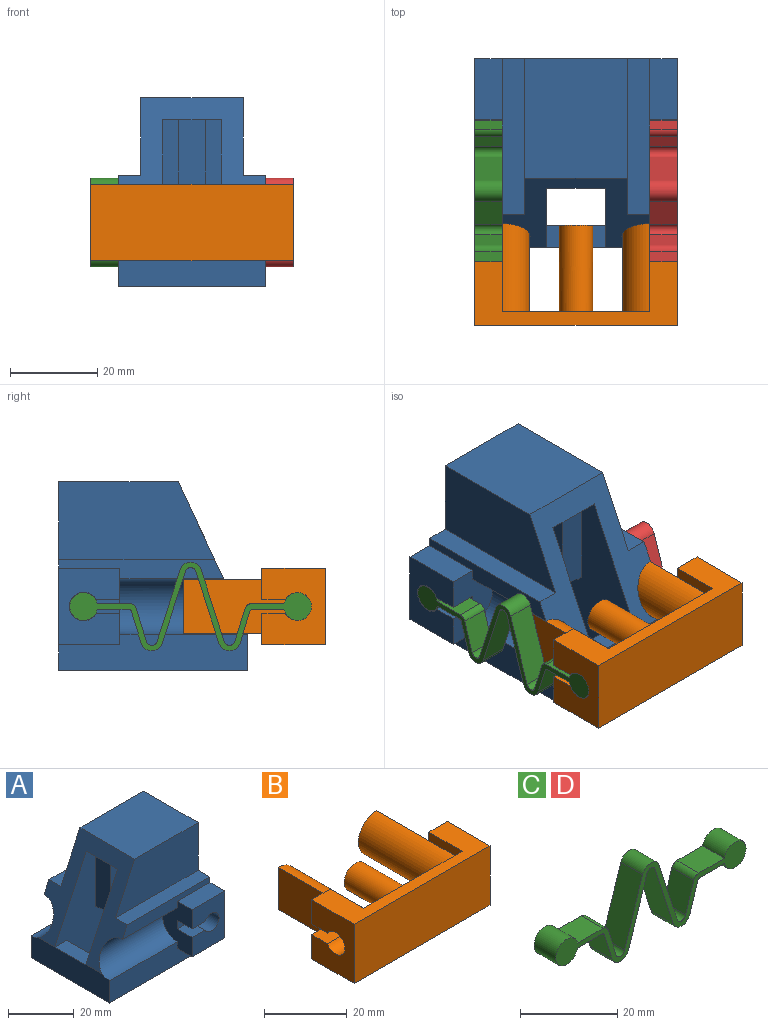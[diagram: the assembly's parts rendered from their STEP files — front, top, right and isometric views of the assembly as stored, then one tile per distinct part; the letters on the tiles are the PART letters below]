
ASSEMBLY  parts=4 mates=6
PART A: 44 faces, bbox 43.2x46.4x43.2 mm
  f0: plane 17.53x12.7mm, normal (-1,0,0), area 154.5mm2, adj f1,f4,f29,f37,f38,f39,f40,f42
  f1: plane 43.23x8.26mm, normal (0,-1,0), area 323mm2, adj f0,f14,f16,f17,f29,f38
  f2: plane 37.72x4.45mm, normal (0,1,0), area 129.2mm2, adj f3,f14,f24,f26,f27,f30
  f3: plane 34.04x33.71mm, normal (-0.91,0,0.42), area 503.5mm2, adj f2,f4,f7,f8,f9,f10,f12,f13
  f4: plane 37.72x4.45mm, normal (0,-1,0), area 129.2mm2, adj f0,f3,f14,f28,f29,f37
  f5: plane 19.05x6.35mm, normal (-1,0,0), area 119.5mm2, adj f6,f13,f18,f19,f21,f23
  f6: plane 8.26x0.99mm, normal (0,0,-1), area 8.2mm2, adj f5,f18,f20,f23
  f7: plane 35.65x17.78mm, normal (0,-1,0), area 560.1mm2, adj f3,f8,f14,f28
  f8: plane 27.36x23.55mm, normal (0,0,1), area 644.1mm2, adj f3,f7,f9,f14
  f9: plane 35.65x17.78mm, normal (0,1,0), area 560.1mm2, adj f3,f8,f14,f24
  f10: plane 38.15x38.1mm, normal (0,1,0), area 1211.5mm2, adj f3,f11,f13,f15,f17,f22
  f11: plane 13.39x9.14mm, normal (1,0,0), area 122.3mm2, adj f10,f12,f17,f22
  f12: plane 38.15x38.1mm, normal (0,-1,0), area 1211.5mm2, adj f3,f11,f13,f15,f17,f22
  f13: plane 24.64x13.39mm, normal (0,0,-1), area 277.5mm2, adj f3,f5,f10,f12,f15,f18,f19,f20
  f14: plane 46.41x43.18mm, normal (1,0,0), area 1497.4mm2, adj f1,f2,f4,f7,f8,f9,f17,f24
  f15: plane 38.1x13.39mm, normal (-1,0,0), area 510mm2, adj f10,f12,f13,f17
  f16: plane 33.71x9.14mm, normal (-1,0,0), area 304.1mm2, adj f1,f3,f17,f22,f25,f26,f29
  f17: plane 43.23x33.71mm, normal (0,0,-1), area 1014.4mm2, adj f1,f10,f11,f12,f14,f15,f16,f25
  f18: plane 19.05x8.26mm, normal (0,-1,0), area 157.3mm2, adj f5,f6,f13,f20
  f19: plane 19.05x8.26mm, normal (0,1,0), area 157.3mm2, adj f5,f13,f20,f21
  f20: plane 19.05x6.35mm, normal (1,0,0), area 119.5mm2, adj f6,f13,f18,f19,f21,f23
  f21: plane 8.26x0.99mm, normal (0,0,-1), area 8.2mm2, adj f5,f19,f20,f23
  f22: plane 13.39x5.08mm, normal (0,0,1), area 68mm2, adj f10,f11,f12,f16
  f23: cylinder r=4.95mm len=8.26mm, axis (-1,0,0), area 37.4mm2, adj f5,f6,f20,f21
  f24: plane 35.65x5.08mm, normal (0,0,1), area 181.1mm2, adj f2,f3,f9,f14
  f25: plane 43.23x8.26mm, normal (0,1,0), area 323mm2, adj f14,f16,f17,f26,f27,f31
  f26: cylinder r=6.35mm len=29.21mm, axis (-1,0,0), area 530.9mm2, adj f2,f3,f16,f25,f27
  f27: plane 17.53x12.7mm, normal (-1,0,0), area 154.5mm2, adj f2,f25,f26,f30,f31,f32,f33,f34
  f28: plane 35.65x5.08mm, normal (0,0,1), area 181.1mm2, adj f3,f4,f7,f14
  f29: cylinder r=6.35mm len=29.21mm, axis (-1,0,0), area 530.9mm2, adj f0,f1,f3,f4,f16
  f30: plane 14.02x6.35mm, normal (0,0,1), area 89mm2, adj f2,f14,f27,f32
  f31: plane 14.02x6.35mm, normal (0,0,-1), area 89mm2, adj f14,f25,f27,f32
  f32: plane 17.53x14.02mm, normal (0,1,0), area 195.4mm2, adj f14,f27,f30,f31,f34,f35,f36
  f33: plane 11.6x6.58mm, normal (0,1,0), area 50.3mm2, adj f27,f34,f35,f36
  f34: plane 6.35x5.43mm, normal (0,0,1), area 34.4mm2, adj f27,f32,f33,f35
  f35: cylinder r=3.29mm len=6.58mm, axis (0,1,0), area 110.2mm2, adj f32,f33,f34,f36
  f36: plane 6.35x5.43mm, normal (0,0,-1), area 34.4mm2, adj f27,f32,f33,f35
  f37: plane 14.02x6.35mm, normal (0,0,1), area 89mm2, adj f0,f4,f14,f39
  f38: plane 14.02x6.35mm, normal (0,0,-1), area 89mm2, adj f0,f1,f14,f39
  f39: plane 17.53x14.02mm, normal (0,-1,0), area 195.4mm2, adj f0,f14,f37,f38,f40,f41,f42
  f40: plane 6.35x5.43mm, normal (0,0,1), area 34.4mm2, adj f0,f39,f41,f43
  f41: cylinder r=3.29mm len=6.58mm, axis (0,-1,0), area 110.2mm2, adj f39,f40,f42,f43
  f42: plane 6.35x5.43mm, normal (0,0,-1), area 34.4mm2, adj f0,f39,f41,f43
  f43: plane 11.6x6.58mm, normal (0,-1,0), area 50.3mm2, adj f0,f40,f41,f42
PART B: 28 faces, bbox 46.4x32.4x17.5 mm
  f0: plane 46.41x14.54mm, normal (0,0,1), area 291.6mm2, adj f2,f3,f4,f11,f14,f15,f18,f24
  f1: plane 11.36x2.54mm, normal (-1,0,0), area 28.9mm2, adj f5,f12,f15,f25
  f2: plane 11.36x2.54mm, normal (-1,0,0), area 28.9mm2, adj f0,f12,f15,f24
  f3: plane 17.53x14.54mm, normal (1,0,0), area 206.7mm2, adj f0,f5,f14,f20,f21,f22,f24,f25
  f4: plane 11.36x2.54mm, normal (1,0,0), area 28.9mm2, adj f0,f10,f15,f18
  f5: plane 46.41x14.54mm, normal (0,0,-1), area 291.6mm2, adj f1,f3,f6,f11,f14,f15,f19,f25
  f6: plane 11.36x2.54mm, normal (1,0,0), area 28.9mm2, adj f5,f10,f15,f19
  f7: plane 12.45x6.22mm, normal (0,1,0), area 60.8mm2, adj f10,f17
  f8: plane 6.35x5.44mm, normal (0,0,1), area 34.5mm2, adj f11,f16,f17,f19
  f9: plane 6.35x5.44mm, normal (0,0,-1), area 34.5mm2, adj f11,f16,f17,f18
  f10: cylinder r=6.22mm len=29.21mm, axis (0,1,0), area 571.1mm2, adj f4,f6,f7,f15,f17
  f11: plane 17.53x14.54mm, normal (-1,0,0), area 206.7mm2, adj f0,f5,f8,f9,f14,f16,f18,f19
  f12: cylinder r=6.22mm len=29.21mm, axis (0,1,0), area 571.1mm2, adj f1,f2,f13,f15,f23
  f13: plane 12.45x6.22mm, normal (0,1,0), area 60.8mm2, adj f12,f23
  f14: plane 46.41x17.53mm, normal (0,-1,0), area 813.3mm2, adj f0,f3,f5,f11
  f15: plane 33.71x17.53mm, normal (0,1,0), area 423.5mm2, adj f0,f1,f2,f4,f5,f6,f10,f12
  f16: cylinder r=3.17mm len=6.35mm, axis (-1,0,0), area 105.6mm2, adj f8,f9,f11,f17
  f17: plane 29.21x12.45mm, normal (-1,0,0), area 270.2mm2, adj f7,f8,f9,f10,f16,f18,f19
  f18: plane 7.18x6.35mm, normal (0,1,0), area 45.6mm2, adj f0,f4,f9,f11,f17
  f19: plane 7.18x6.35mm, normal (0,1,0), area 45.6mm2, adj f5,f6,f8,f11,f17
  f20: plane 6.35x5.44mm, normal (0,0,1), area 34.5mm2, adj f3,f22,f23,f25
  f21: plane 6.35x5.44mm, normal (0,0,-1), area 34.5mm2, adj f3,f22,f23,f24
  f22: cylinder r=3.17mm len=6.35mm, axis (1,0,0), area 105.6mm2, adj f3,f20,f21,f23
  f23: plane 29.21x12.45mm, normal (1,0,0), area 270.2mm2, adj f12,f13,f20,f21,f22,f24,f25
  f24: plane 7.18x6.35mm, normal (0,1,0), area 45.6mm2, adj f0,f2,f3,f21,f23
  f25: plane 7.18x6.35mm, normal (0,1,0), area 45.6mm2, adj f1,f3,f5,f20,f23
  f26: cylinder r=3.81mm len=19.69mm, axis (0,-1,0), area 471.2mm2, adj f15,f27
  f27: plane 7.62x7.62mm, normal (0,1,0), area 45.6mm2, adj f26
PART C: 26 faces, bbox 55.3x6.4x20.3 mm
  f0: cylinder r=3.17mm len=6.35mm, axis (0,1,0), area 118.6mm2, adj f1,f23,f24,f25
  f1: plane 7.09x6.35mm, normal (0,0,-1), area 45mm2, adj f0,f2,f24,f25
  f2: cylinder r=0.76mm len=6.35mm, axis (0,1,0), area 6.1mm2, adj f1,f3,f24,f25
  f3: plane 7.2x6.35mm, normal (-0.96,0,-0.3), area 47.9mm2, adj f2,f4,f24,f25
  f4: cylinder r=2.54mm len=6.35mm, axis (0,1,0), area 40.8mm2, adj f3,f5,f24,f25
  f5: plane 16.4x6.35mm, normal (0.95,0,-0.31), area 109.4mm2, adj f4,f6,f24,f25
  f6: cylinder r=1.27mm len=6.35mm, axis (0,1,0), area 20.3mm2, adj f5,f7,f24,f25
  f7: plane 16.4x6.35mm, normal (-0.95,0,-0.31), area 109.4mm2, adj f6,f8,f24,f25
  f8: cylinder r=2.54mm len=6.35mm, axis (0,1,0), area 40.8mm2, adj f7,f9,f24,f25
  f9: plane 7.2x6.35mm, normal (0.96,0,-0.3), area 47.9mm2, adj f8,f10,f24,f25
  f10: cylinder r=0.76mm len=6.35mm, axis (0,1,0), area 6.1mm2, adj f9,f11,f24,f25
  f11: plane 7.09x6.35mm, normal (0,0,-1), area 45mm2, adj f10,f12,f24,f25
  f12: cylinder r=3.17mm len=6.35mm, axis (0,1,0), area 118.6mm2, adj f11,f13,f24,f25
  f13: plane 7.46x6.35mm, normal (0,0,1), area 47.4mm2, adj f12,f14,f24,f25
  f14: cylinder r=1.52mm len=6.35mm, axis (0,1,0), area 12.3mm2, adj f13,f15,f24,f25
  f15: plane 7.56x6.35mm, normal (-0.96,0,0.3), area 50.2mm2, adj f14,f16,f24,f25
  f16: cylinder r=1.27mm len=6.35mm, axis (0,1,0), area 20.4mm2, adj f15,f17,f24,f25
  f17: plane 16.4x6.35mm, normal (0.95,0,0.31), area 109.4mm2, adj f16,f18,f24,f25
  f18: cylinder r=2.54mm len=6.35mm, axis (0,1,0), area 40.7mm2, adj f17,f19,f24,f25
  f19: plane 16.4x6.35mm, normal (-0.95,0,0.31), area 109.4mm2, adj f18,f20,f24,f25
  f20: cylinder r=1.27mm len=6.35mm, axis (0,1,0), area 20.4mm2, adj f19,f21,f24,f25
  f21: plane 7.56x6.35mm, normal (0.96,0,0.3), area 50.2mm2, adj f20,f22,f24,f25
  f22: cylinder r=1.52mm len=6.35mm, axis (0,1,0), area 12.3mm2, adj f21,f23,f24,f25
  f23: plane 7.46x6.35mm, normal (0,0,1), area 47.4mm2, adj f0,f22,f24,f25
  f24: plane 55.3x20.32mm, normal (0,-1,0), area 167.4mm2, adj f0,f1,f2,f3,f4,f5,f6,f7
  f25: plane 55.3x20.32mm, normal (0,1,0), area 167.4mm2, adj f0,f1,f2,f3,f4,f5,f6,f7
PART D: same geometry as C
PLACE A rot(axis=(0,0,1),90deg) t=(0,-21.62,-43.18)mm
PLACE B t=(0,-28.63,-28.58)mm
PLACE C rot(axis=(0,0,-1),90deg) t=(-16.85,-30.19,-28.58)mm
PLACE D rot(axis=(0,0,-1),90deg) t=(23.2,-30.19,-28.57)mm
MATE slider A.f41 <-> A.f41  axis (1,0,0) through (23.2,-5.72,-28.57)mm
MATE fastened C.f12 <-> B.f16  axis (1,0,0) through (-20.03,-54.66,-28.58)mm
MATE planar D.f0 <-> A.f41  axis (1,0,0) through (23.2,-5.72,-28.57)mm
MATE cylindrical C.f0 <-> A.f35  axis (-1,0,0) through (-23.2,-5.71,-28.58)mm
MATE slider A.f26 <-> B.f10  axis (0,-1,0) through (-16.85,-28.63,-28.58)mm
MATE slider D.f12 <-> B.f22  axis (1,0,0) through (20.03,-54.66,-28.57)mm
